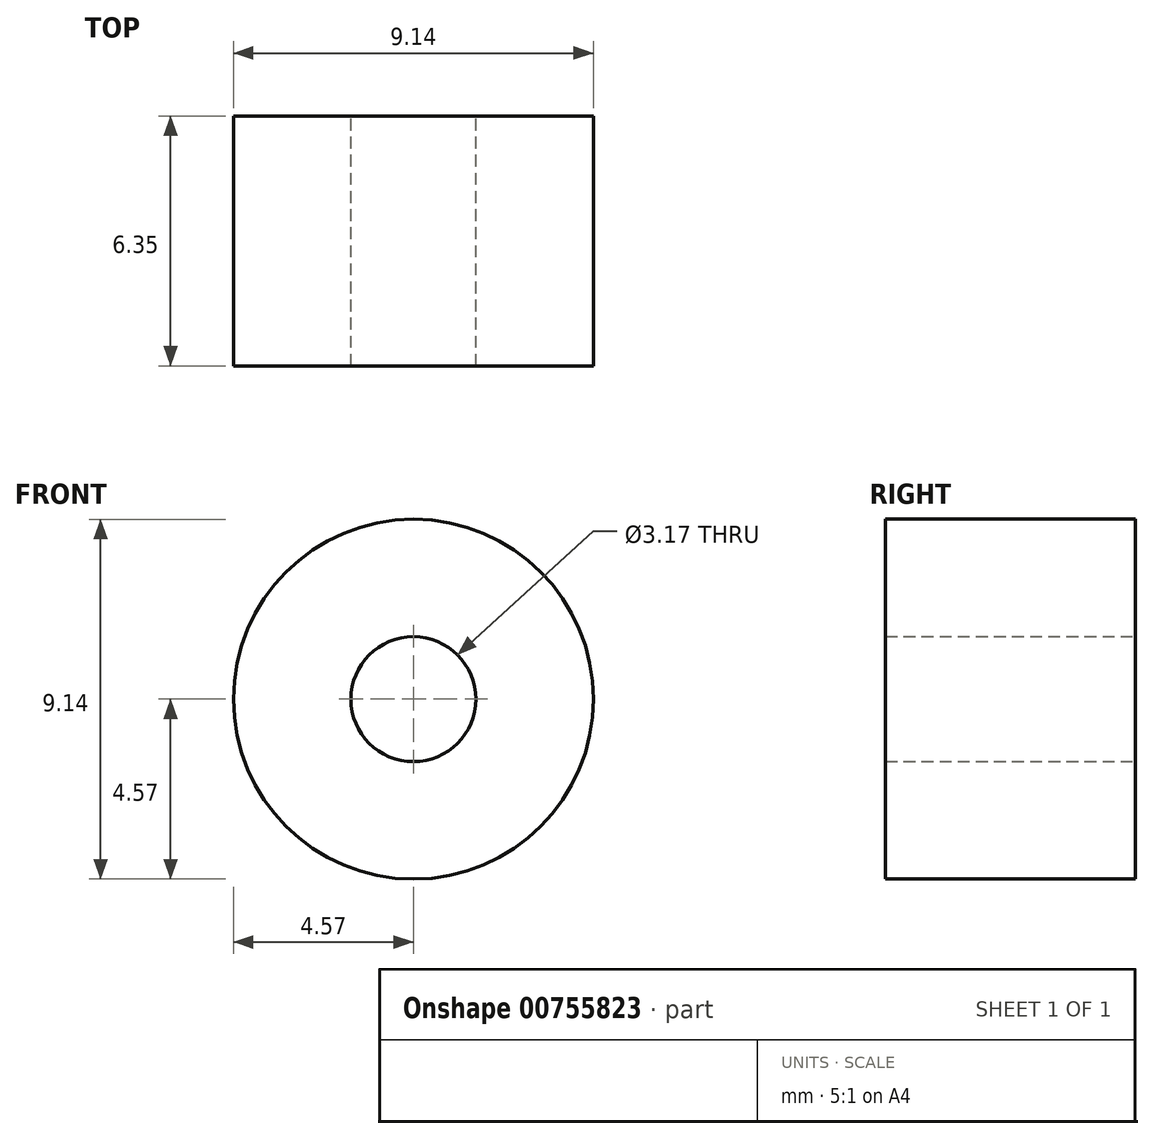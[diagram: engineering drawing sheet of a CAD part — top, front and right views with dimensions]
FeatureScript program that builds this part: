
annotation { "Feature Type Name" : "Feature", "Feature Type Description" : "" }
export const myFeature = defineFeature(function(context is Context, id is Id, definition is map)
    precondition{}
    {
        {
            var Q0;
            Q0=qCreatedBy(makeId("Front.planeOp"),FACE);
            var sketch = newSketch(context, id + "F0", { "sketchPlane" : qUnion([Q0])});
            skCircle(sketch, "E0", {"center": v(0, 0) * mm, "radius": 4.57 * mm});
            skCircle(sketch, "E1", {"center": v(0, 0) * mm, "radius": 1.59 * mm});
            skSolve(sketch);
        }
        {
            var Q0;
            Q0 = qSketchRegion(id + "F0", true);
            extrude(context, id + "F1", {"entities" : qUnion([Q0]), "depth" : 6.35 * mm, "offsetDistance" : 25.4 * mm});
        }
    });
